# Revit family: IS_Tesi_T3522_BIM_BE
name_source: partatom
category: Plumbing Fixtures
revit_build: Autodesk Revit 2015 (Build: 20140606_1530(x64)
units: mm (PartAtom-declared; Revit-internal decimal feet)

## types (1)
- T352201 - Tesi Lavabo 60cm LIGHT, emballage carton
    Accesoires = www.idealstandard.be
    Afwerking = Wit
    Auteur = Ideal Standard Produktions-GmbH
    Barcode = 8014140430278
    Beschrijvinggarantie = Fabrieksgarantie
    BimObjectNaam = ISI_IdealStandard_Lavabo_Tesi_T352201
    Breedte = 0
    BrutoGewicht = 0
    Cost = 0 $
    Default Elevation = 850 mm
    Description = Tesi Lavabo 60cm LIGHT, emballage carton
    Diepte = 0 mm  [stored 0 ft]
    Dimensions = 476 x 605 x 169 mm
    DuurEenheid = jaar
    Eigenschappen = Tesi wastafel in porselein. 1 kraangat in het midden doorgestoken
    Garantieonderdelen = 10
    GrootteAfvoergat = 0
    Hauteur = 169 mm
    IfcExportAs = IfcSanitaryTerminalType
    IfcExportType = WASHHANDBASINS
    Installatieinstructies = www.idealstandard.be
    Kleur = Wit
    Largeur = 605 mm
    Lengte = 0 mm  [stored 0 ft]
    Longueur = 476 mm
    Manufacturer = www.idealstandard.be
    Materiaal = porselein
    Merk = Ideal Standard
    Model = T352201
    Nettogewicht = 15.8
    Ophangingwastafel = muurbevestiging
    Productinformatie = www.idealstandard.be
    Telefoonnummer = 0032 2 325 66 00
    Typeconnectie = Sanitair
    Typewastafel = wastafel
    URL = www.idealstandard.be
    Uniclass2015Beschrijving = Wash basins, sinks and troughs
    Uniclass2015Referentie = Pr_40_20_96
    Uniclass2015Version = Products v1.1
    Urlproducent = www.idealstandard.be
    Versie = 1
    Vervangingskosten = 0
    Verwachtelevensduur = 25 jaar
    Volumeunits = liter

note: [stored X ft] marks values corroborated as IEEE doubles in the binary element streams (Revit-internal decimal feet)

## geometry (parser evidence)
native form markers: Blend x4, Sweep x1
no freeform markers — native parametric forms only
